# Revit family: NewTechWood-UltraEasy_Fencing-Gate
name_source: partatom
category: Specialty Equipment
units: mm (PartAtom-declared; Revit-internal decimal feet)

## family parameters
Always vertical = Yes
Cut with Voids When Loaded = No
Enable Cutting in Views = No
Maintain Annotation Orientation = No
Part Type = Normal
Room Calculation Point = No
Round Connector Dimension = Use Diameter
Shared = No
Work Plane-Based = No

## types (1)
- UH66
    Construction Details = https://www.arcat.com
    Default Elevation = 0 "
    Description = UltraShield® Naturale™ UltraEasy Fence Gate, 38" Width x 72" Height x 1.125" Thickness, With Capped Composite Board, 6" Height x 0.8" Thickness x 34" Width
    Frame Thickness = 1 "
    Gate Height = 72 "
    Installation-Fabrication = https://www.newtechwood.com
    Manufacturer = NewTechWood America Inc.
    Manufacturer Fax = 1-281-661-1167
    Model = Fence Gate UH66
    Panel Length = 38 "
    Panel Thickness = 1 "
    Post Center To Post Center = 42 "
    Post Height = 75 "
    Product Data = https://www.arcat.com
    Sales Information = https://www.newtechwood.com
    URL = https://www.newtechwood.com
    Width = 38 "

## geometry (parser evidence)
native form markers: Sweep x6
no freeform markers — native parametric forms only
